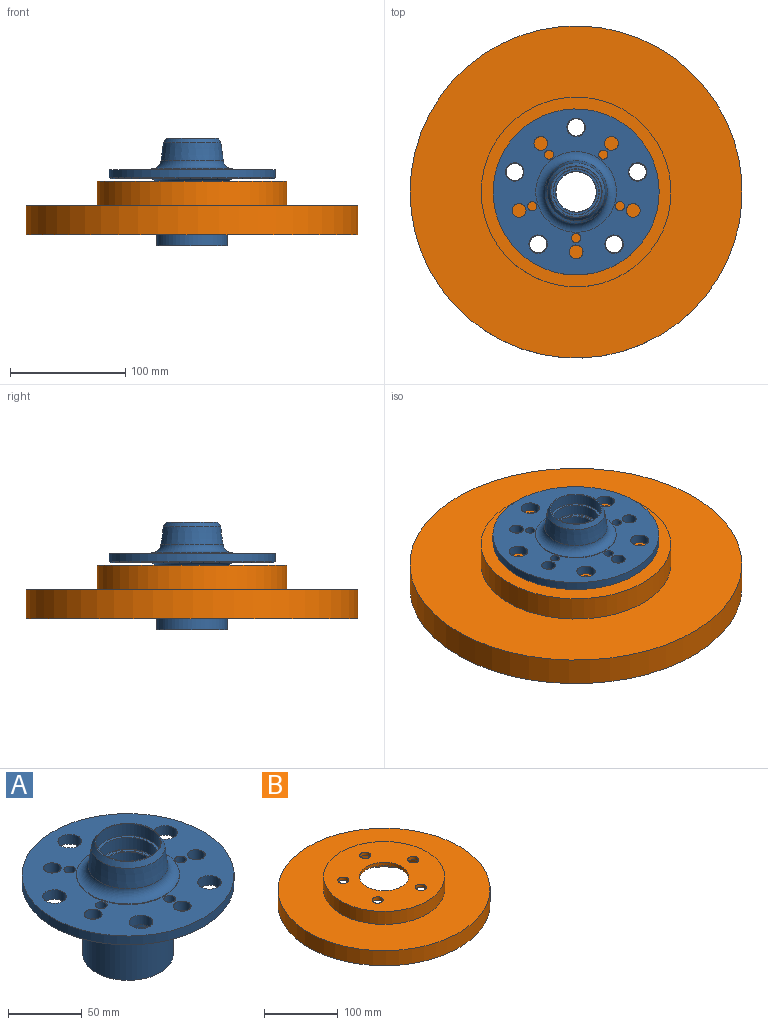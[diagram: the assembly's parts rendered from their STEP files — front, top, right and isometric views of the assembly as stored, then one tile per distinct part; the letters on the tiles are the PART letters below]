
ASSEMBLY  parts=2 mates=1
PART A: 46 faces, bbox 144x144x93 mm
  f0: cylinder r=20mm len=40mm, axis (0,0,1), area 1218.9mm2, adj f38,f44
  f1: cone r=77mm half-angle=56.3deg, axis (0,0,1), area 539.9mm2, adj f37,f42
  f2: cylinder r=4mm len=8mm, axis (0,0,1), area 201.1mm2, adj f17,f42
  f3: cylinder r=4mm len=8mm, axis (0,0,1), area 201.1mm2, adj f17,f42
  f4: cylinder r=4mm len=8mm, axis (0,0,1), area 201.1mm2, adj f17,f42
  f5: cylinder r=4mm len=8mm, axis (0,0,1), area 201.1mm2, adj f17,f42
  f6: cylinder r=4mm len=8mm, axis (0,0,1), area 201.1mm2, adj f17,f42
  f7: cylinder r=8mm len=16mm, axis (0,0,1), area 402.1mm2, adj f17,f42
  f8: cylinder r=8mm len=16mm, axis (0,0,1), area 402.1mm2, adj f17,f42
  f9: cylinder r=8mm len=16mm, axis (0,0,1), area 402.1mm2, adj f17,f42
  f10: cylinder r=8mm len=16mm, axis (0,0,1), area 402.1mm2, adj f17,f42
  f11: cylinder r=8mm len=16mm, axis (0,0,1), area 402.1mm2, adj f17,f42
  f12: cylinder r=6mm len=12mm, axis (0,0,1), area 301.6mm2, adj f17,f42
  f13: cylinder r=6mm len=12mm, axis (0,0,1), area 301.6mm2, adj f17,f42
  f14: cylinder r=6mm len=12mm, axis (0,0,1), area 301.6mm2, adj f17,f42
  f15: cylinder r=6mm len=12mm, axis (0,0,1), area 301.6mm2, adj f17,f42
  f16: cylinder r=6mm len=12mm, axis (0,0,1), area 301.6mm2, adj f17,f42
  f17: plane 144x144mm, normal (0,0,1), area 10615.4mm2, adj f2,f3,f4,f5,f6,f7,f8,f9
  f18: cylinder r=17.5mm len=35mm, axis (0,0,1), area 1143.5mm2, adj f39,f40
  f19: plane 61.4x61.4mm, normal (0,0,-1), area 133.5mm2, adj f20,f36
  f20: cylinder r=30.7mm len=61.4mm, axis (0,0,1), area 8294.4mm2, adj f19,f21
  f21: plane 62x62mm, normal (0,0,-1), area 58.2mm2, adj f20,f22
  f22: cylinder r=31mm len=62mm, axis (0,0,1), area 1947.8mm2, adj f21,f43
  f23: cylinder r=35mm len=70mm, axis (0,0,1), area 110mm2, adj f17,f24
  f24: torus R=35mm, axis (0,0,1), area 2202mm2, adj f23,f25
  f25: cone r=25mm half-angle=7.4deg, axis (0,0,-1), area 2547.9mm2, adj f24,f26
  f26: cone r=22.5mm half-angle=32deg, axis (0,0,-1), area 703.9mm2, adj f25,f27
  f27: plane 45x45mm, normal (0,0,1), area 69.9mm2, adj f26,f35
  f28: plane 39.4x39.4mm, normal (0,0,1), area 223.8mm2, adj f38,f39
  f29: plane 58x58mm, normal (0,0,-1), area 678.6mm2, adj f30,f32
  f30: cylinder r=29mm len=58mm, axis (0,0,-1), area 1731mm2, adj f29,f36
  f31: plane 50x50mm, normal (0,0,-1), area 373.1mm2, adj f32,f34
  f32: cylinder r=25mm len=50mm, axis (0,0,-1), area 1727.9mm2, adj f29,f31
  f33: plane 44.4x44.4mm, normal (0,0,-1), area 552.9mm2, adj f40,f41
  f34: cylinder r=22.5mm len=45mm, axis (0,0,-1), area 5753.8mm2, adj f31,f41
  f35: cone r=20mm half-angle=45deg, axis (0,0,1), area 2mm2, adj f27,f45
  f36: cone r=29mm half-angle=63.4deg, axis (0,0,-1), area 207.2mm2, adj f19,f30
  f37: cylinder r=72mm len=144mm, axis (0,0,1), area 3317.5mm2, adj f1,f17
  f38: cone r=19.7mm half-angle=45deg, axis (0,0,1), area 52.9mm2, adj f0,f28
  f39: cone r=17.5mm half-angle=45deg, axis (0,0,1), area 47.1mm2, adj f18,f28
  f40: cone r=17.8mm half-angle=45deg, axis (0,0,-1), area 47.1mm2, adj f18,f33
  f41: cone r=22.2mm half-angle=45deg, axis (0,0,-1), area 59.6mm2, adj f33,f34
  f42: plane 142x142mm, normal (0,0,-1), area 9943.1mm2, adj f1,f2,f3,f4,f5,f6,f7,f8
  f43: torus R=36mm, axis (0,0,-1), area 1619.4mm2, adj f22,f42
  f44: plane 43.98x43.98mm, normal (0,0,1), area 262.5mm2, adj f0,f45
  f45: cylinder r=21.99mm len=43.98mm, axis (0,0,1), area 1380.3mm2, adj f35,f44
PART B: 15 faces, bbox 288x288x46.5 mm
  f0: cylinder r=144mm len=288mm, axis (0,0,-1), area 22619.5mm2, adj f1,f2
  f1: plane 288x288mm, normal (0,0,1), area 43865.1mm2, adj f0,f3
  f2: plane 288x288mm, normal (0,0,-1), area 40538.3mm2, adj f0,f6
  f3: cylinder r=82.3mm len=164.6mm, axis (0,0,-1), area 11117.8mm2, adj f1,f4
  f4: plane 164.6x164.6mm, normal (0,0,1), area 16869.7mm2, adj f3,f9,f10,f11,f12,f13,f14
  f5: plane 177x177mm, normal (0,0,-1), area 5906.6mm2, adj f6,f8
  f6: cylinder r=88.5mm len=177mm, axis (0,0,-1), area 4448.5mm2, adj f2,f5
  f7: plane 154.3x154.3mm, normal (0,0,-1), area 14289.9mm2, adj f8,f9,f10,f11,f12,f13,f14
  f8: cylinder r=77.15mm len=154.3mm, axis (0,0,-1), area 15996.7mm2, adj f5,f7
  f9: cylinder r=33.5mm len=67mm, axis (0,0,1), area 1157.7mm2, adj f4,f7
  f10: cylinder r=7.5mm len=15mm, axis (0,0,1), area 259.2mm2, adj f4,f7
  f11: cylinder r=7.5mm len=15mm, axis (0,0,1), area 259.2mm2, adj f4,f7
  f12: cylinder r=7.5mm len=15mm, axis (0,0,1), area 259.2mm2, adj f4,f7
  f13: cylinder r=7.5mm len=15mm, axis (0,0,1), area 259.2mm2, adj f4,f7
  f14: cylinder r=7.5mm len=15mm, axis (0,0,1), area 259.2mm2, adj f4,f7
PLACE A t=(0,-0.39,8.92)mm fixed
PLACE B rot(axis=(0,0,1),18deg) t=(0,-0.39,-37.58)mm
MATE cylindrical B.f9 <-> A.f20  axis (0,0,1) through (0,-0.39,6.17)mm
